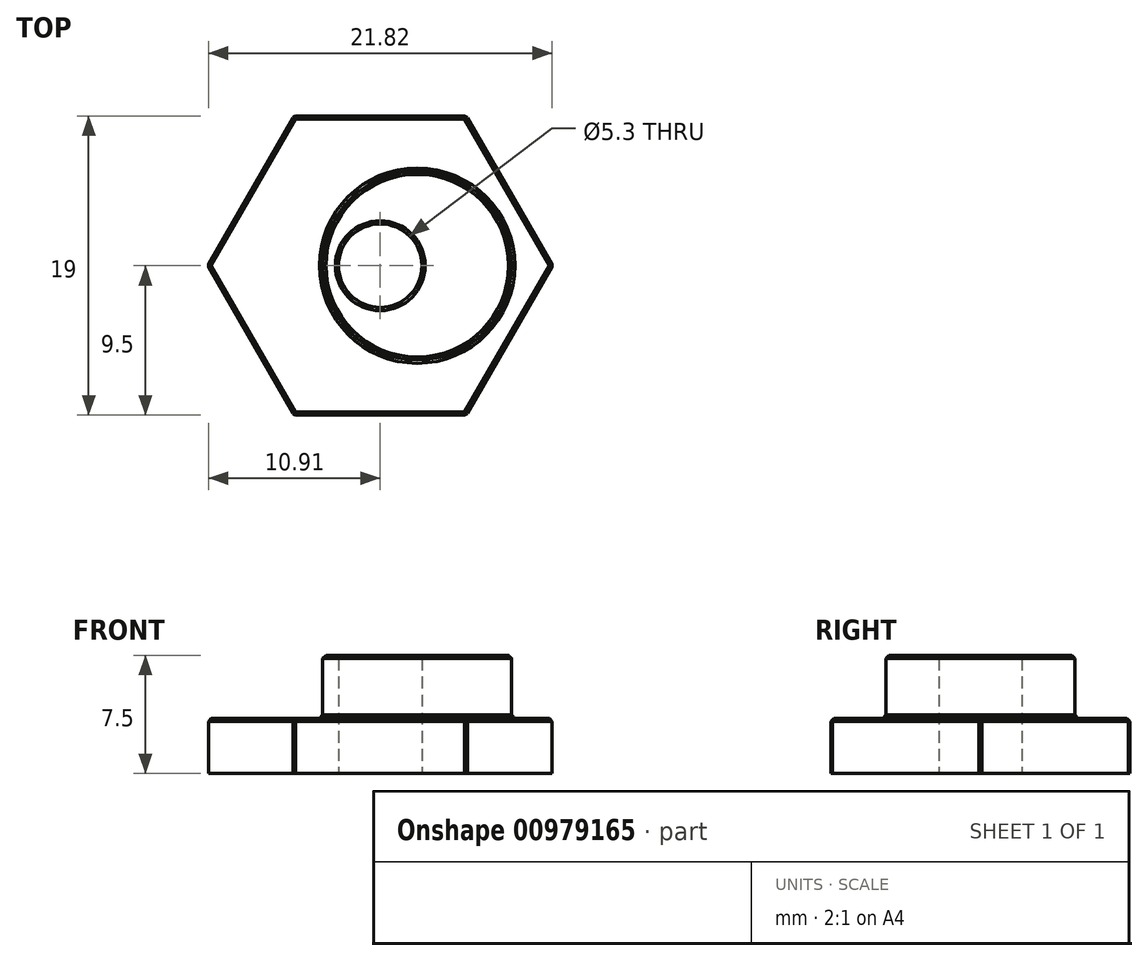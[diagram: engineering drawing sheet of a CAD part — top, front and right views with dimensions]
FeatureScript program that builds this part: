
annotation { "Feature Type Name" : "Feature", "Feature Type Description" : "" }
export const myFeature = defineFeature(function(context is Context, id is Id, definition is map)
    precondition{}
    {
        {
            var Q0;
            Q0=qCreatedBy(makeId("Top.planeOp"),FACE);
            var sketch = newSketch(context, id + "F0", { "sketchPlane" : qUnion([Q0])});
            skCircle(sketch, "E0.cCircle", {"center": v(0, 0) * mm, "radius": 9.5 * mm, "construction": true});
            skLineSegment(sketch, "E0.0", {"start": v(-5.48, 9.5) * mm, "end": v(5.48, 9.5) * mm});
            skLineSegment(sketch, "E0.1", {"start": v(5.48, 9.5) * mm, "end": v(10.97, 0) * mm});
            skLineSegment(sketch, "E0.2", {"start": v(10.97, 0) * mm, "end": v(5.48, -9.5) * mm});
            skLineSegment(sketch, "E0.3", {"start": v(5.48, -9.5) * mm, "end": v(-5.48, -9.5) * mm});
            skLineSegment(sketch, "E0.4", {"start": v(-5.48, -9.5) * mm, "end": v(-10.97, 0) * mm});
            skLineSegment(sketch, "E0.5", {"start": v(-10.97, 0) * mm, "end": v(-5.48, 9.5) * mm});
            skPoint(sketch, "E0.0.midPoint", {"position": v(0, 9.5) * mm});
            skSolve(sketch);
        }
        {
            var Q0;
            Q0=makeQuery(id+"F0.imprint","IMPRINT",FACE,{"disambiguationData":[TD([[makeQuery(id+"F0.imprint","IMPRINT",EDGE,{"derivedFrom":sQuery(id+"F0.wireOp",EDGE,"E0.0")}),-1.0]])]});
            extrude(context, id + "F1", {"entities" : qUnion([Q0]), "depth" : 3.5 * mm, "offsetDistance" : 25 * mm});
        }
        {
            var Q0;
            Q0=makeQuery(id+"F1.opExtrude","CAP_FACE",FACE,{"disambiguationData":[OSD([sQuery(id+"F0.wireOp",EDGE,"E0.0"),sQuery(id+"F0.wireOp",EDGE,"E0.1"),sQuery(id+"F0.wireOp",EDGE,"E0.2"),sQuery(id+"F0.wireOp",EDGE,"E0.3"),sQuery(id+"F0.wireOp",EDGE,"E0.4"),sQuery(id+"F0.wireOp",EDGE,"E0.5")])],"isStart":false});
            var sketch = newSketch(context, id + "F2", { "sketchPlane" : qUnion([Q0])});
            skCircle(sketch, "E1", {"center": v(2.35, 0) * mm, "radius": 6 * mm});
            skSolve(sketch);
        }
        {
            var Q0;
            Q0 = qSketchRegion(id + "F2", true);
            extrude(context, id + "F3", {"entities" : qUnion([Q0]), "operationType" : NewBodyOperationType.ADD, "depth" : 4 * mm, "offsetDistance" : 25 * mm});
        }
        {
            var Q0;
            Q0=makeQuery(id+"F1.opExtrude","CAP_FACE",FACE,{"disambiguationData":[OSD([sQuery(id+"F0.wireOp",EDGE,"E0.0"),sQuery(id+"F0.wireOp",EDGE,"E0.1"),sQuery(id+"F0.wireOp",EDGE,"E0.2"),sQuery(id+"F0.wireOp",EDGE,"E0.3"),sQuery(id+"F0.wireOp",EDGE,"E0.4"),sQuery(id+"F0.wireOp",EDGE,"E0.5")])],"isStart":true});
            var sketch = newSketch(context, id + "F4", { "sketchPlane" : qUnion([Q0])});
            skCircle(sketch, "E2", {"center": v(0, 0) * mm, "radius": 2.65 * mm});
            skSolve(sketch);
        }
        {
            var Q0;
            Q0 = qSketchRegion(id + "F4", true);
            extrude(context, id + "F5", {"entities" : qUnion([Q0]), "operationType" : NewBodyOperationType.REMOVE, "oppositeDirection" : true, "depth" : 25 * mm, "offsetDistance" : 25 * mm});
        }
        {
            var Q0;
            Q0=makeQuery(id+"F3.opExtrude","CAP_EDGE",EDGE,{"disambiguationData":[OSD([sQuery(id+"F2.wireOp",EDGE,"E1")])],"isStart":false});
            var Q1;
            Q1=makeQuery(id+"F5.boolean.opBoolean","INTERSECT",EDGE,{"derivedFrom":[makeQuery(id+"F3.opExtrude","CAP_FACE",FACE,{"disambiguationData":[OSD([sQuery(id+"F2.wireOp",EDGE,"E1")])],"isStart":false}),makeQuery(id+"F5.opExtrude","SWEPT_FACE",FACE,{"disambiguationData":[OSD([sQuery(id+"F4.wireOp",EDGE,"E2")])]})]});
            var Q2;
            Q2=makeQuery(id+"F1.opExtrude","CAP_EDGE",EDGE,{"disambiguationData":[OSD([sQuery(id+"F0.wireOp",EDGE,"E0.2")])],"isStart":false});
            var Q3;
            Q3=makeQuery(id+"F1.opExtrude","CAP_EDGE",EDGE,{"disambiguationData":[OSD([sQuery(id+"F0.wireOp",EDGE,"E0.3")])],"isStart":false});
            var Q4;
            Q4=makeQuery(id+"F1.opExtrude","CAP_FACE",FACE,{"disambiguationData":[OSD([sQuery(id+"F0.wireOp",EDGE,"E0.0"),sQuery(id+"F0.wireOp",EDGE,"E0.1"),sQuery(id+"F0.wireOp",EDGE,"E0.2"),sQuery(id+"F0.wireOp",EDGE,"E0.3"),sQuery(id+"F0.wireOp",EDGE,"E0.4"),sQuery(id+"F0.wireOp",EDGE,"E0.5")])],"isStart":false});
            var Q5;
            Q5=makeQuery(id+"F1.opExtrude","SWEPT_EDGE",EDGE,{"disambiguationData":[OSD([sQuery(id+"F0.wireOp",EDGE,"E0.1"),sQuery(id+"F0.wireOp",EDGE,"E0.2")])]});
            var Q6;
            Q6=makeQuery(id+"F1.opExtrude","SWEPT_EDGE",EDGE,{"disambiguationData":[OSD([sQuery(id+"F0.wireOp",EDGE,"E0.2"),sQuery(id+"F0.wireOp",EDGE,"E0.3")])]});
            var Q7;
            Q7=makeQuery(id+"F1.opExtrude","SWEPT_EDGE",EDGE,{"disambiguationData":[OSD([sQuery(id+"F0.wireOp",EDGE,"E0.0"),sQuery(id+"F0.wireOp",EDGE,"E0.1")])]});
            var Q8;
            Q8=makeQuery(id+"F1.opExtrude","SWEPT_EDGE",EDGE,{"disambiguationData":[OSD([sQuery(id+"F0.wireOp",EDGE,"E0.0"),sQuery(id+"F0.wireOp",EDGE,"E0.5")])]});
            var Q9;
            Q9=makeQuery(id+"F1.opExtrude","SWEPT_EDGE",EDGE,{"disambiguationData":[OSD([sQuery(id+"F0.wireOp",EDGE,"E0.4"),sQuery(id+"F0.wireOp",EDGE,"E0.5")])]});
            var Q10;
            Q10=makeQuery(id+"F1.opExtrude","SWEPT_EDGE",EDGE,{"disambiguationData":[OSD([sQuery(id+"F0.wireOp",EDGE,"E0.3"),sQuery(id+"F0.wireOp",EDGE,"E0.4")])]});
            chamfer(context, id + "F6", {"entities" : qUnion([Q0, Q1, Q2, Q3, Q4, Q5, Q6, Q7, Q8, Q9, Q10]), "width" : 0.2 * mm, "tangentPropagation" : true});
        }
    });
